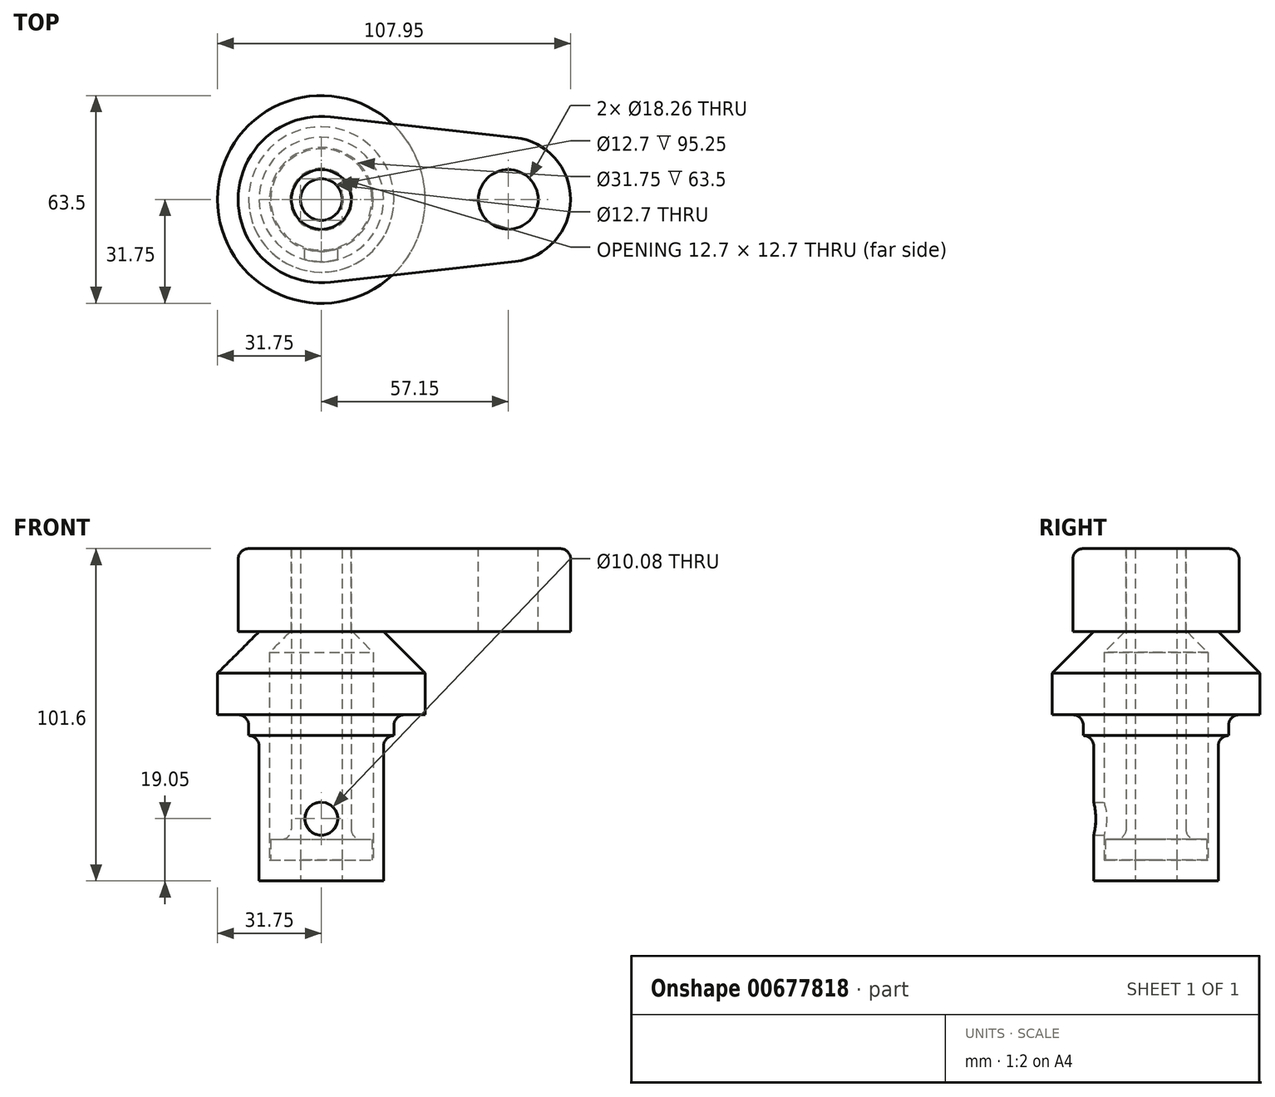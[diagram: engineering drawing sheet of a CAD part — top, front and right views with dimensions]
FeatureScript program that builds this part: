
annotation { "Feature Type Name" : "Feature", "Feature Type Description" : "" }
export const myFeature = defineFeature(function(context is Context, id is Id, definition is map)
    precondition{}
    {
        {
            var Q0;
            Q0=qCreatedBy(makeId("Front.planeOp"),FACE);
            var sketch = newSketch(context, id + "F0", { "sketchPlane" : qUnion([Q0])});
            skLineSegment(sketch, "E0", {"start": v(0, 0) * mm, "end": v(0, 76.2) * mm});
            skLineSegment(sketch, "E1", {"start": v(0, 76.2) * mm, "end": v(19.05, 76.2) * mm});
            skLineSegment(sketch, "E2", {"start": v(19.05, 76.2) * mm, "end": v(31.75, 63.5) * mm});
            skLineSegment(sketch, "E3", {"start": v(31.75, 63.5) * mm, "end": v(31.75, 50.8) * mm});
            skLineSegment(sketch, "E4", {"start": v(31.75, 50.8) * mm, "end": v(22.23, 50.8) * mm});
            skLineSegment(sketch, "E5", {"start": v(22.23, 50.8) * mm, "end": v(22.23, 44.45) * mm});
            skLineSegment(sketch, "E6", {"start": v(22.23, 44.45) * mm, "end": v(19.05, 44.45) * mm});
            skLineSegment(sketch, "E7", {"start": v(19.05, 44.45) * mm, "end": v(19.05, 0) * mm});
            skLineSegment(sketch, "E8", {"start": v(19.05, 0) * mm, "end": v(0, 0) * mm});
            skLineSegment(sketch, "E9", {"start": v(9.52, 76.2) * mm, "end": v(15.88, 69.85) * mm});
            skLineSegment(sketch, "E10", {"start": v(15.88, 69.85) * mm, "end": v(15.88, 6.35) * mm});
            skLineSegment(sketch, "E11", {"start": v(15.88, 6.35) * mm, "end": v(0, 6.35) * mm});
            skLineSegment(sketch, "E12", {"start": v(0, 76.2) * mm, "end": v(0, 91.41) * mm, "construction": true});
            skLineSegment(sketch, "E13", {"start": v(0, 76.2) * mm, "end": v(0, 101.6) * mm});
            skLineSegment(sketch, "E14", {"start": v(0, 101.6) * mm, "end": v(9.13, 101.6) * mm});
            skLineSegment(sketch, "E15", {"start": v(9.13, 101.6) * mm, "end": v(9.13, 12.7) * mm});
            skLineSegment(sketch, "E16", {"start": v(9.13, 12.7) * mm, "end": v(15.48, 12.7) * mm});
            skLineSegment(sketch, "E17", {"start": v(15.48, 12.7) * mm, "end": v(15.48, 6.35) * mm});
            skSolve(sketch);
        }
        {
            var Q0;
            {var subQ4=sQuery(id+"F0.wireOp",EDGE,"E2");Q0=makeQuery(id+"F0.imprint","IMPRINT",FACE,{"disambiguationData":[TD([[makeQuery(id+"F0.imprint","IMPRINT",EDGE,{"derivedFrom":subQ4}),-1.0]])]});}
            var Q1;
            Q1=sQuery(id+"F0.wireOp",EDGE,"E0");
            revolve(context, id + "F1", {"entities" : qUnion([Q0]), "axis" : qUnion([Q1]), "revolveType" : RevolveType.FULL});
        }
        {
            var Q0;
            {var subQ0=sQuery(id+"F0.wireOp",EDGE,"E13");Q0=makeQuery(id+"F0.imprint","IMPRINT",FACE,{"disambiguationData":[TD([[makeQuery(id+"F0.imprint","IMPRINT",EDGE,{"derivedFrom":subQ0}),-1.0]])]});}
            var Q1;
            {var subQ0=sQuery(id+"F0.wireOp",EDGE,"E16");Q1=makeQuery(id+"F0.imprint","IMPRINT",FACE,{"disambiguationData":[TD([[makeQuery(id+"F0.imprint","IMPRINT",EDGE,{"derivedFrom":subQ0}),-1.0]])]});}
            var Q2;
            Q2=sQuery(id+"F0.wireOp",EDGE,"E13");
            revolve(context, id + "F2", {"entities" : qUnion([Q0, Q1]), "axis" : qUnion([Q2]), "revolveType" : RevolveType.FULL});
        }
        {
            var Q0;
            Q0=makeQuery(id+"F2.opRevolve","SWEPT_FACE",FACE,{"disambiguationData":[OSD([sQuery(id+"F0.wireOp",EDGE,"E14")])]});
            var sketch = newSketch(context, id + "F3", { "sketchPlane" : qUnion([Q0])});
            skCircle(sketch, "E18", {"center": v(0, 0) * mm, "radius": 25.4 * mm});
            skCircle(sketch, "E19", {"center": v(57.15, 0) * mm, "radius": 19.05 * mm});
            skLineSegment(sketch, "E20", {"start": v(2.82, 25.24) * mm, "end": v(59.27, 18.93) * mm});
            skLineSegment(sketch, "E21", {"start": v(2.82, -25.24) * mm, "end": v(59.27, -18.93) * mm});
            skCircle(sketch, "E22.0", {"center": v(0, 0) * mm, "radius": 9.13 * mm});
            skCircle(sketch, "E23", {"center": v(57.15, 0) * mm, "radius": 9.13 * mm});
            skSolve(sketch);
        }
        {
            var Q0;
            Q0 = qSketchRegion(id + "F3", true);
            var Q1;
            Q1=makeQuery(id+"F1.opRevolve","SWEPT_FACE",FACE,{"disambiguationData":[OSD([sQuery(id+"F0.wireOp",EDGE,"E1")])]});
            extrude(context, id + "F4", {"entities" : qUnion([Q0]), "oppositeDirection" : true, "depth" : 25.4 * mm, "endBoundEntityFace" : qUnion([Q1]), "offsetDistance" : 1 / 406.4 * mm});
        }
        {
            var Q0;
            Q0=qCreatedBy(makeId("Front.planeOp"),FACE);
            var sketch = newSketch(context, id + "F5", { "sketchPlane" : qUnion([Q0])});
            skPoint(sketch, "E24", {"position": v(0, 19.05) * mm});
            skSolve(sketch);
        }
        {
            var Q0;
            Q0=sQuery(id+"F5.wireOp",VERTEX,"E24");
            var Q1;
            Q1=makeQuery(id+"F1.opRevolve","SWEPT_BODY",BODY,{"disambiguationData":[OSD([sQuery(id+"F0.wireOp",EDGE,"E0"),sQuery(id+"F0.wireOp",EDGE,"E1"),sQuery(id+"F0.wireOp",EDGE,"E2"),sQuery(id+"F0.wireOp",EDGE,"E3"),sQuery(id+"F0.wireOp",EDGE,"E4"),sQuery(id+"F0.wireOp",EDGE,"E5"),sQuery(id+"F0.wireOp",EDGE,"E6"),sQuery(id+"F0.wireOp",EDGE,"E7"),sQuery(id+"F0.wireOp",EDGE,"E8"),sQuery(id+"F0.wireOp",EDGE,"E9"),sQuery(id+"F0.wireOp",EDGE,"E10"),sQuery(id+"F0.wireOp",EDGE,"E11")])]});
            hole(context, id + "F6", {"style" : HoleStyle.SIMPLE, "endStyle" : HoleEndStyle.THROUGH, "oppositeDirection" : true, "standardTappedOrClearance" : lookupTablePath({ "standard" : "ANSI", "fit" : "Normal (ASME)", "size" : "3/8", "type" : "Clearance" }), "standardBlindInLast" : lookupTablePath({ "fit" : "Free", "standard" : "ANSI", "size" : "3/8", "type" : "Clearance" }), "holeDiameter" : 10.08 * mm, "majorDiameter" : 6.35 * mm, "tappedDepth" : 14.3 * mm, "tapClearance" : 3, "locations" : qUnion([Q0]), "scope" : qUnion([Q1])});
        }
        {
            var Q0;
            Q0=makeQuery(id+"F4.opExtrude","CAP_EDGE",EDGE,{"disambiguationData":[OSD([sQuery(id+"F3.wireOp",EDGE,"E20")])],"isStart":true});
            var Q1;
            Q1=makeQuery(id+"F1.opRevolve","SWEPT_EDGE",EDGE,{"disambiguationData":[OSD([sQuery(id+"F0.wireOp",EDGE,"E4"),sQuery(id+"F0.wireOp",EDGE,"E5")])]});
            var Q2;
            Q2=makeQuery(id+"F1.opRevolve","SWEPT_EDGE",EDGE,{"disambiguationData":[OSD([sQuery(id+"F0.wireOp",EDGE,"E6"),sQuery(id+"F0.wireOp",EDGE,"E7")])]});
            var Q3;
            Q3=makeQuery(id+"F2.opRevolve","SWEPT_EDGE",EDGE,{"disambiguationData":[OSD([sQuery(id+"F0.wireOp",EDGE,"E15"),sQuery(id+"F0.wireOp",EDGE,"E16")])]});
            fillet(context, id + "F7", {"entities" : qUnion([Q0, Q1, Q2, Q3]), "radius" : 3.17 * mm, "tangentPropagation" : true, "allowEdgeOverflow" : false});
        }
        {
            var Q0;
            Q0=makeQuery(id+"F1.opRevolve","SWEPT_FACE",FACE,{"disambiguationData":[OSD([sQuery(id+"F0.wireOp",EDGE,"E8")])]});
            var sketch = newSketch(context, id + "F8", { "sketchPlane" : qUnion([Q0])});
            skCircle(sketch, "E25", {"center": v(0, 0) * mm, "radius": 6.35 * mm});
            skSolve(sketch);
        }
        {
            var Q0;
            Q0 = qSketchRegion(id + "F8", true);
            extrude(context, id + "F9", {"entities" : qUnion([Q0]), "operationType" : NewBodyOperationType.REMOVE, "endBound" : BoundingType.THROUGH_ALL, "oppositeDirection" : true, "depth" : 25.4 * mm, "offsetDistance" : 25.4 * mm});
        }
    });
